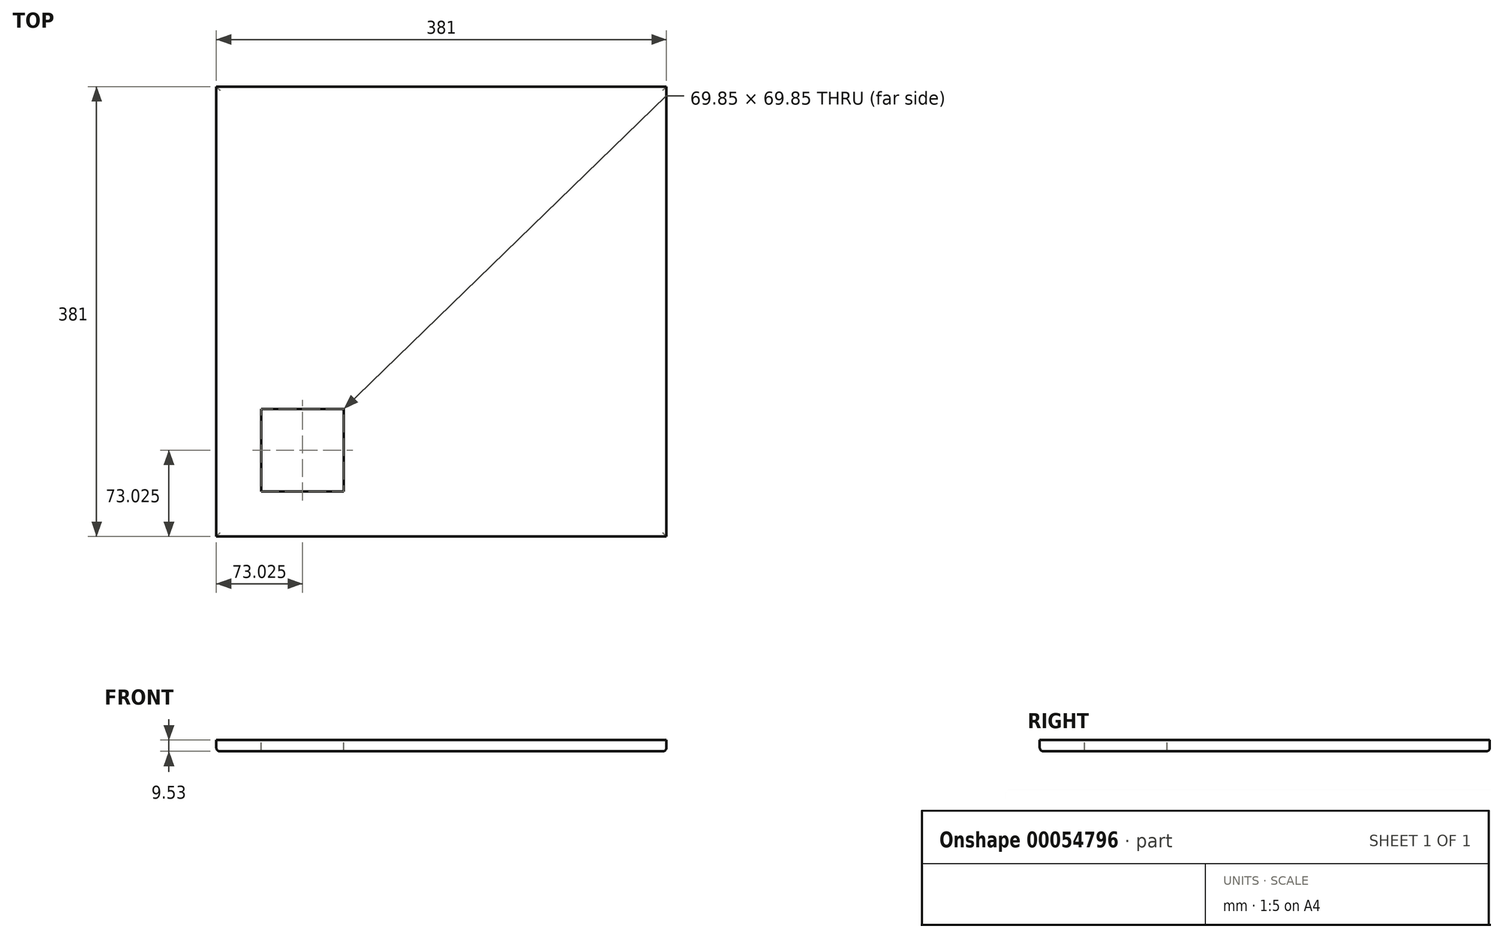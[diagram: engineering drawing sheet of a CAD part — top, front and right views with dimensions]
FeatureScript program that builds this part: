
annotation { "Feature Type Name" : "Feature", "Feature Type Description" : "" }
export const myFeature = defineFeature(function(context is Context, id is Id, definition is map)
    precondition{}
    {
        {
            var Q0;
            Q0=qCreatedBy(makeId("Top.planeOp"),FACE);
            var sketch = newSketch(context, id + "F0", { "sketchPlane" : qUnion([Q0])});
            skLineSegment(sketch, "E0.bottom", {"start": v(0, 0) * mm, "end": v(381, 0) * mm});
            skLineSegment(sketch, "E0.top", {"start": v(0, 381) * mm, "end": v(381, 381) * mm});
            skLineSegment(sketch, "E0.left", {"start": v(0, 0) * mm, "end": v(0, 381) * mm});
            skLineSegment(sketch, "E0.right", {"start": v(381, 0) * mm, "end": v(381, 381) * mm});
            skSolve(sketch);
        }
        {
            var Q0;
            Q0=makeQuery(id+"F0.imprint","IMPRINT",FACE,{"disambiguationData":[TD([[makeQuery(id+"F0.imprint","IMPRINT",EDGE,{"derivedFrom":sQuery(id+"F0.wireOp",EDGE,"E0.bottom")}),1.0]])]});
            extrude(context, id + "F1", {"entities" : qUnion([Q0]), "depth" : 9.52 * mm});
        }
        {
            var Q0;
            Q0=makeQuery(id+"F1.opExtrude","CAP_FACE",FACE,{"disambiguationData":[OSD([sQuery(id+"F0.wireOp",EDGE,"E0.bottom"),sQuery(id+"F0.wireOp",EDGE,"E0.top"),sQuery(id+"F0.wireOp",EDGE,"E0.left"),sQuery(id+"F0.wireOp",EDGE,"E0.right")])],"isStart":false});
            var sketch = newSketch(context, id + "F2", { "sketchPlane" : qUnion([Q0])});
            skLineSegment(sketch, "E1.bottom", {"start": v(38.1, 38.1) * mm, "end": v(107.95, 38.1) * mm});
            skLineSegment(sketch, "E1.top", {"start": v(38.1, 107.95) * mm, "end": v(107.95, 107.95) * mm});
            skLineSegment(sketch, "E1.left", {"start": v(38.1, 38.1) * mm, "end": v(38.1, 107.95) * mm});
            skLineSegment(sketch, "E1.right", {"start": v(107.95, 38.1) * mm, "end": v(107.95, 107.95) * mm});
            skSolve(sketch);
        }
        {
            var Q0;
            Q0=makeQuery(id+"F2.imprint","IMPRINT",FACE,{"disambiguationData":[TD([[makeQuery(id+"F2.imprint","IMPRINT",EDGE,{"derivedFrom":sQuery(id+"F2.wireOp",EDGE,"E1.bottom")}),1.0]])]});
            extrude(context, id + "F3", {"entities" : qUnion([Q0]), "operationType" : NewBodyOperationType.REMOVE, "endBound" : BoundingType.UP_TO_NEXT, "oppositeDirection" : true, "depth" : 25.4 * mm});
        }
        {
            var Q0;
            Q0=makeQuery(id+"F1.opExtrude","CAP_EDGE",EDGE,{"disambiguationData":[OSD([sQuery(id+"F0.wireOp",EDGE,"E0.left")])],"isStart":true});
            var Q1;
            Q1=makeQuery(id+"F1.opExtrude","CAP_EDGE",EDGE,{"disambiguationData":[OSD([sQuery(id+"F0.wireOp",EDGE,"E0.bottom")])],"isStart":true});
            var Q2;
            Q2=makeQuery(id+"F1.opExtrude","CAP_EDGE",EDGE,{"disambiguationData":[OSD([sQuery(id+"F0.wireOp",EDGE,"E0.right")])],"isStart":true});
            var Q3;
            Q3=makeQuery(id+"F1.opExtrude","CAP_EDGE",EDGE,{"disambiguationData":[OSD([sQuery(id+"F0.wireOp",EDGE,"E0.top")])],"isStart":true});
            fillet(context, id + "F4", {"entities" : qUnion([Q0, Q1, Q2, Q3]), "radius" : 3.17 * mm, "tangentPropagation" : true, "allowEdgeOverflow" : false});
        }
    });
